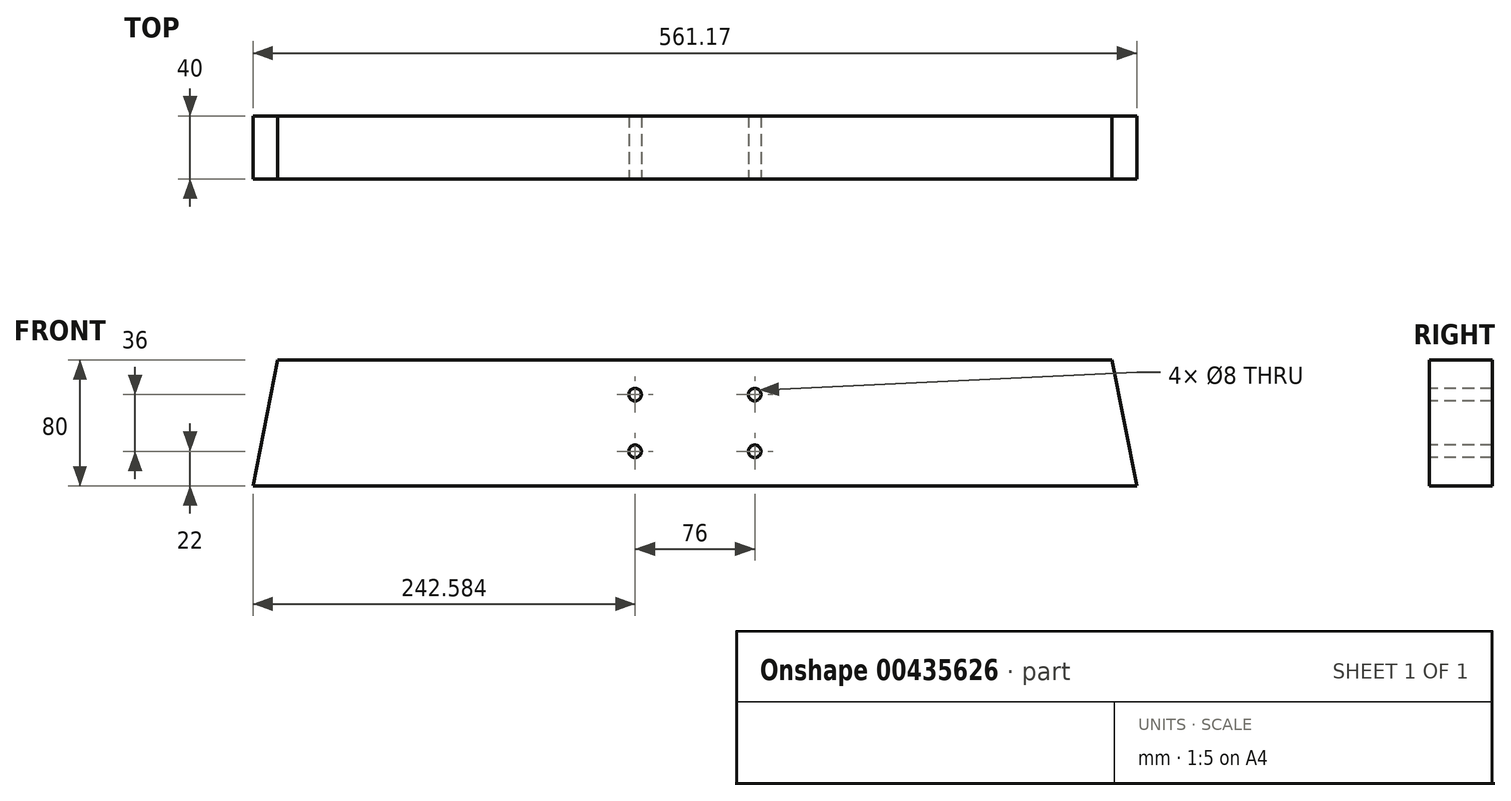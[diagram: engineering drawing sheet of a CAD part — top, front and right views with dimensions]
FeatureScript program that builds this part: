
annotation { "Feature Type Name" : "Feature", "Feature Type Description" : "" }
export const myFeature = defineFeature(function(context is Context, id is Id, definition is map)
    precondition{}
    {
        {
            var Q0;
            Q0=qCreatedBy(makeId("Front.planeOp"),FACE);
            var sketch = newSketch(context, id + "F0", { "sketchPlane" : qUnion([Q0])});
            skLineSegment(sketch, "E0.bottom", {"start": v(15.58, 0) * mm, "end": v(545.58, 0) * mm});
            skLineSegment(sketch, "E0.top", {"start": v(0, -80) * mm, "end": v(561.17, -80) * mm});
            skLineSegment(sketch, "E1", {"start": v(0, -80) * mm, "end": v(15.58, 0) * mm});
            skLineSegment(sketch, "E2", {"start": v(0, -80) * mm, "end": v(-96.54, -80) * mm, "construction": true});
            skLineSegment(sketch, "E3", {"start": v(561.17, -80) * mm, "end": v(545.58, 0) * mm});
            skLineSegment(sketch, "E4", {"start": v(561.17, -80) * mm, "end": v(631.94, -80) * mm, "construction": true});
            skLineSegment(sketch, "E5", {"start": v(280.58, 99.1) * mm, "end": v(280.58, -163.02) * mm, "construction": true});
            skLineSegment(sketch, "E6", {"start": v(199.54, -40) * mm, "end": v(376.55, -40) * mm, "construction": true});
            skPoint(sketch, "E6.startSnap0", {"position": v(7.8, -40) * mm});
            skLineSegment(sketch, "E7.bottom", {"start": v(242.58, -22) * mm, "end": v(318.58, -22) * mm, "construction": true});
            skLineSegment(sketch, "E7.top", {"start": v(242.58, -58) * mm, "end": v(318.58, -58) * mm, "construction": true});
            skLineSegment(sketch, "E7.left", {"start": v(242.58, -22) * mm, "end": v(242.58, -58) * mm, "construction": true});
            skLineSegment(sketch, "E7.right", {"start": v(318.58, -22) * mm, "end": v(318.58, -58) * mm, "construction": true});
            skCircle(sketch, "E8", {"center": v(242.58, -22) * mm, "radius": 4 * mm});
            skCircle(sketch, "E9", {"center": v(318.58, -22) * mm, "radius": 4 * mm});
            skCircle(sketch, "E10", {"center": v(318.58, -58) * mm, "radius": 4 * mm});
            skCircle(sketch, "E11", {"center": v(242.58, -58) * mm, "radius": 4 * mm});
            skSolve(sketch);
        }
        {
            var Q0;
            Q0 = qSketchRegion(id + "F0", true);
            extrude(context, id + "F1", {"entities" : qUnion([Q0]), "oppositeDirection" : true, "depth" : 40 * mm});
        }
    });
